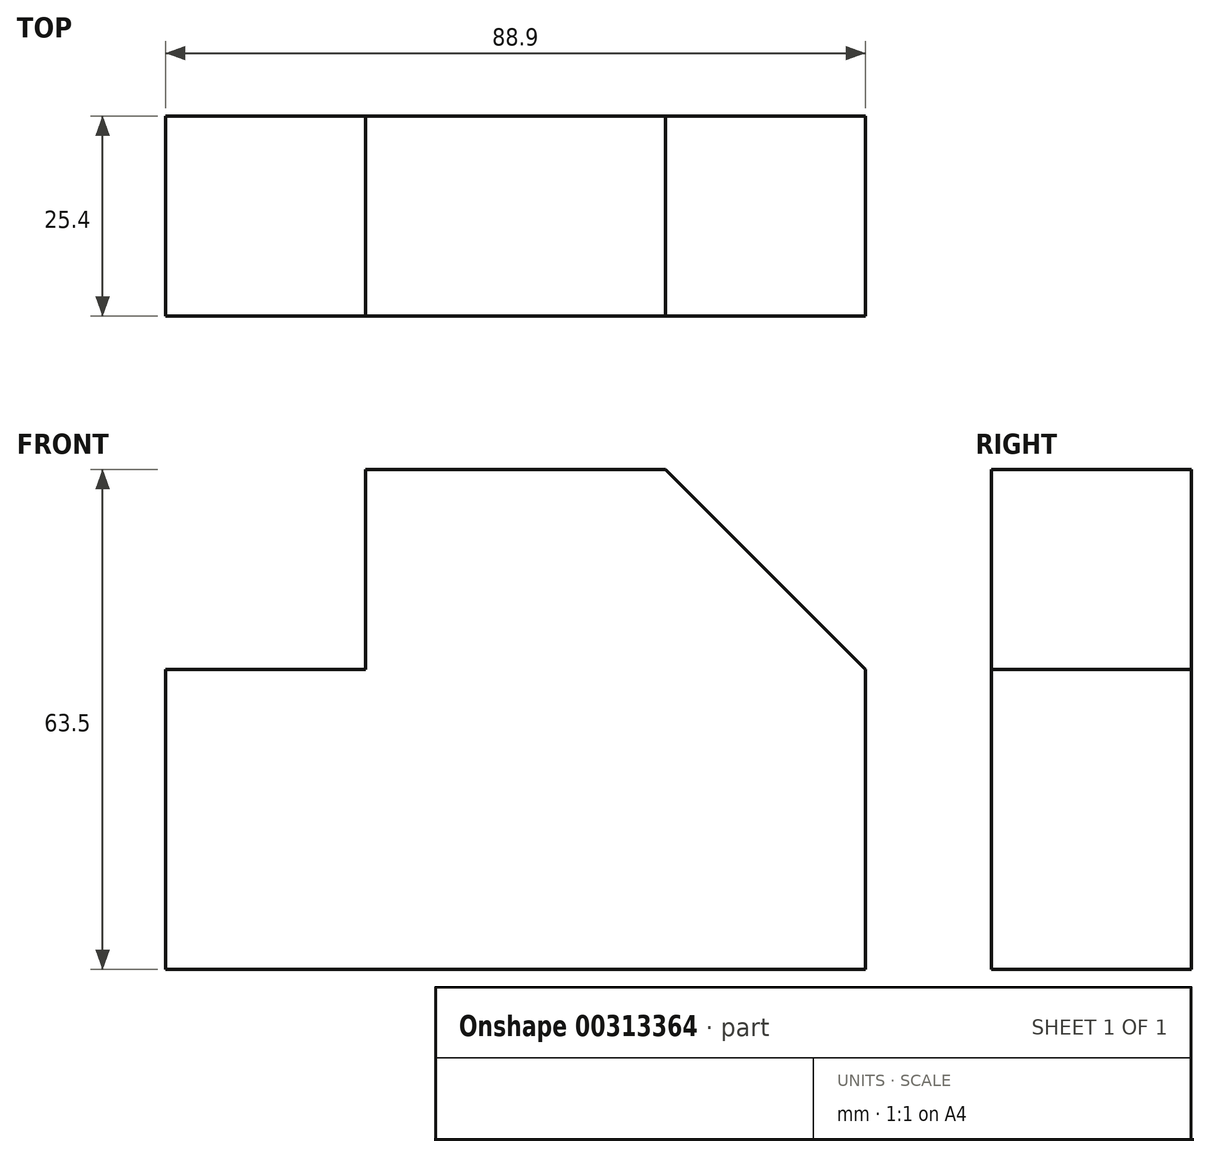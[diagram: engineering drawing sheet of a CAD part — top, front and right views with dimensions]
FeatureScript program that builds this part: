
annotation { "Feature Type Name" : "Feature", "Feature Type Description" : "" }
export const myFeature = defineFeature(function(context is Context, id is Id, definition is map)
    precondition{}
    {
        {
            var Q0;
            Q0=qCreatedBy(makeId("Front.planeOp"),FACE);
            var sketch = newSketch(context, id + "F0", { "sketchPlane" : qUnion([Q0])});
            skLineSegment(sketch, "E0", {"start": v(-38.57, -17.23) * mm, "end": v(50.33, -17.23) * mm});
            skLineSegment(sketch, "E1", {"start": v(50.33, -17.23) * mm, "end": v(50.33, 20.87) * mm});
            skLineSegment(sketch, "E2", {"start": v(-38.57, -17.23) * mm, "end": v(-38.57, 20.87) * mm});
            skLineSegment(sketch, "E3", {"start": v(-38.57, 20.87) * mm, "end": v(-13.17, 20.87) * mm});
            skLineSegment(sketch, "E4", {"start": v(-13.17, 20.87) * mm, "end": v(-13.17, 46.27) * mm});
            skLineSegment(sketch, "E5", {"start": v(-13.17, 46.27) * mm, "end": v(24.93, 46.27) * mm});
            skLineSegment(sketch, "E6", {"start": v(24.93, 46.27) * mm, "end": v(50.33, 20.87) * mm});
            skSolve(sketch);
        }
        {
            var Q0;
            Q0=makeQuery(id+"F0.imprint","IMPRINT",FACE,{"disambiguationData":[TD([[makeQuery(id+"F0.imprint","IMPRINT",EDGE,{"derivedFrom":sQuery(id+"F0.wireOp",EDGE,"E0")}),1.0]])]});
            extrude(context, id + "F1", {"entities" : qUnion([Q0]), "depth" : 25.4 * mm});
        }
    });
